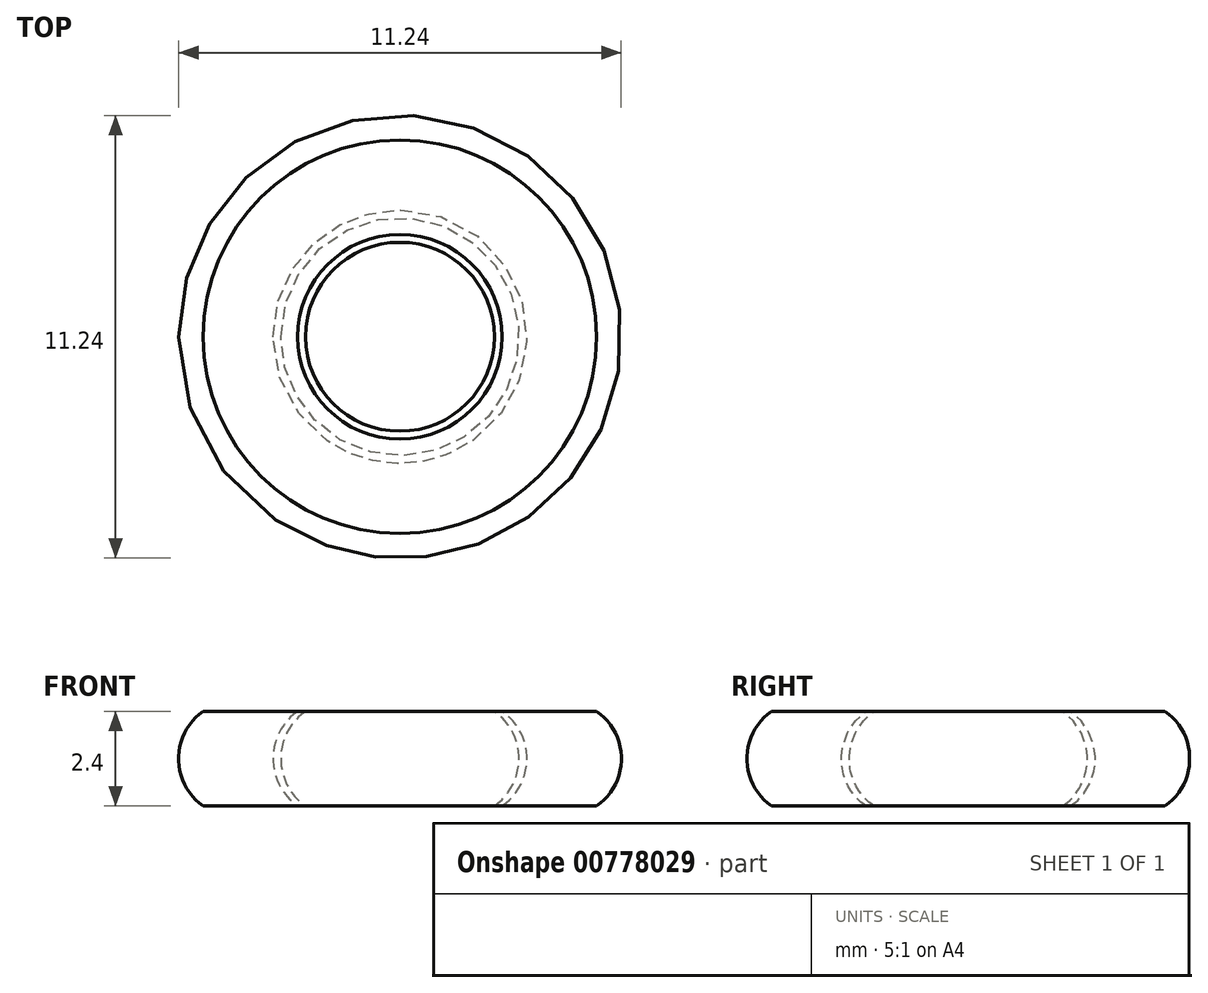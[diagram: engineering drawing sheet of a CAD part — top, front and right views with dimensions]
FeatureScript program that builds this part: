
annotation { "Feature Type Name" : "Feature", "Feature Type Description" : "" }
export const myFeature = defineFeature(function(context is Context, id is Id, definition is map)
    precondition{}
    {
        {
            var Q0;
            Q0=qCreatedBy(makeId("Front.planeOp"),FACE);
            var sketch = newSketch(context, id + "F0", { "sketchPlane" : qUnion([Q0])});
            skArc(sketch, "E0", {"start": v(-2.4, 2.4) * mm, "mid": v(-3.02, 1.2) * mm, "end": v(-2.4, 0) * mm});
            skLineSegment(sketch, "E1", {"start": v(-2.4, 0) * mm, "end": v(-4.02, 1.13) * mm, "construction": true});
            skLineSegment(sketch, "E2", {"start": v(0, 0) * mm, "end": v(0, 2.4) * mm});
            skLineSegment(sketch, "E3", {"start": v(0, 0) * mm, "end": v(-2.4, 0) * mm});
            skLineSegment(sketch, "E4", {"start": v(-2.4, 2.4) * mm, "end": v(0, 2.4) * mm});
            skLineSegment(sketch, "E5", {"start": v(-2.6, 0) * mm, "end": v(-5, 0) * mm});
            skArc(sketch, "E6", {"start": v(-2.6, 2.4) * mm, "mid": v(-3.22, 1.2) * mm, "end": v(-2.6, 0) * mm});
            skArc(sketch, "E7", {"start": v(-5, 2.4) * mm, "mid": v(-5.62, 1.2) * mm, "end": v(-5, 0) * mm});
            skLineSegment(sketch, "E8", {"start": v(-5, 2.4) * mm, "end": v(-2.6, 2.4) * mm});
            skSolve(sketch);
        }
        {
            var Q0;
            Q0=makeQuery(id+"F0.imprint","IMPRINT",FACE,{"disambiguationData":[TD([[makeQuery(id+"F0.imprint","IMPRINT",EDGE,{"derivedFrom":sQuery(id+"F0.wireOp",EDGE,"E0")}),1.0]])]});
            var Q1;
            Q1=makeQuery(id+"F0.imprint","IMPRINT",FACE,{"disambiguationData":[TD([[makeQuery(id+"F0.imprint","IMPRINT",EDGE,{"derivedFrom":sQuery(id+"F0.wireOp",EDGE,"E5")}),-1.0]])]});
            var Q2;
            Q2=sQuery(id+"F0.wireOp",EDGE,"E2");
            revolve(context, id + "F1", {"surfaceOperationType" : NewSurfaceOperationType.NEW, "entities" : qUnion([Q0, Q1]), "axis" : qUnion([Q2]), "revolveType" : RevolveType.FULL});
        }
    });
